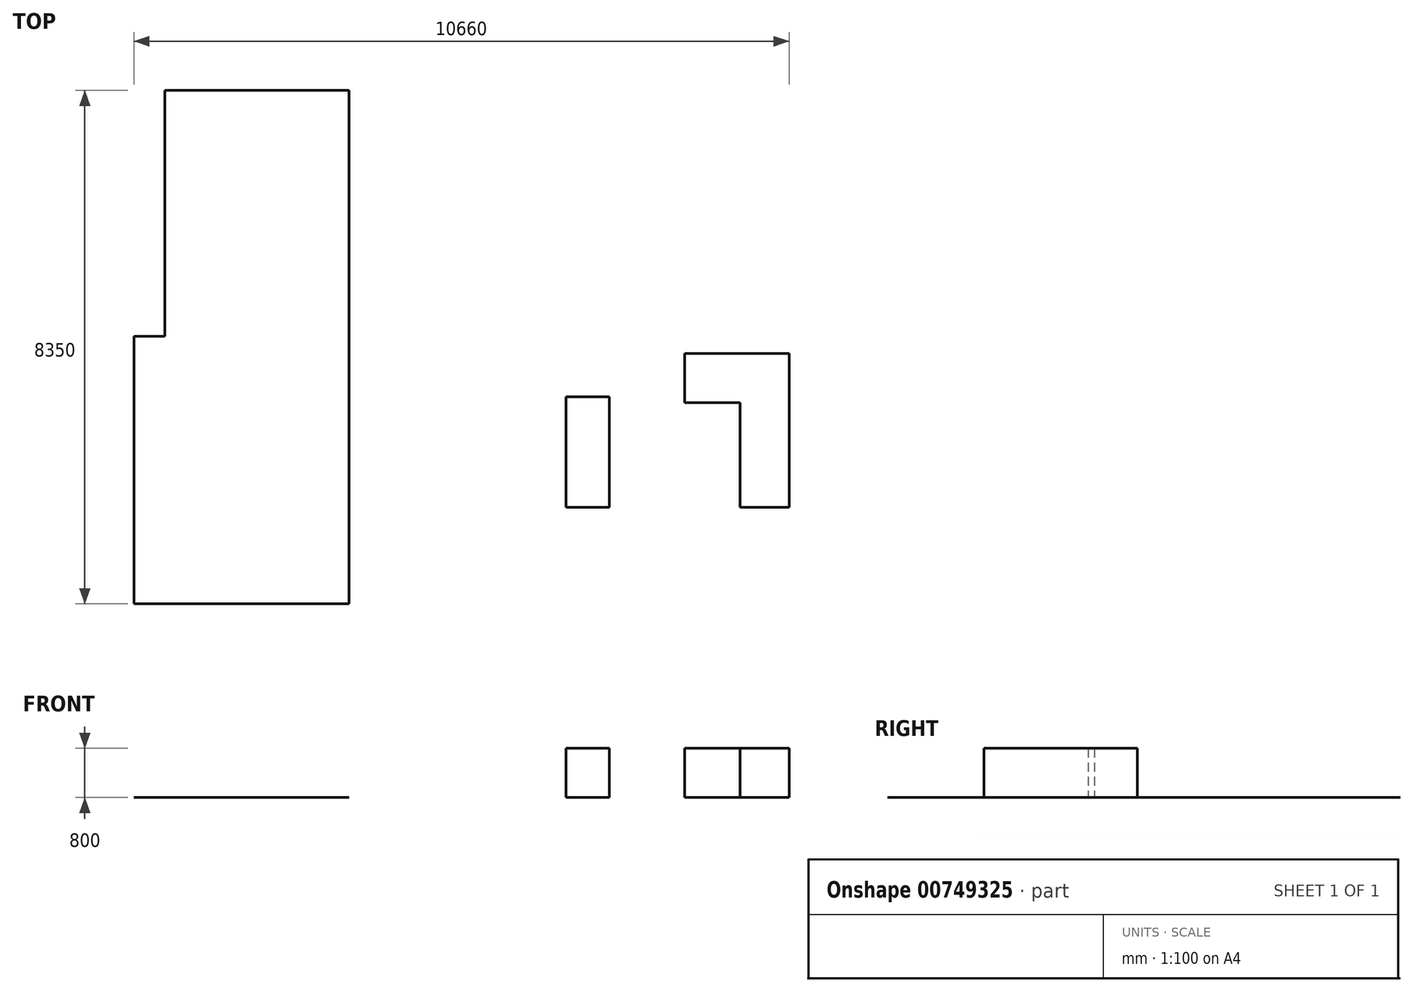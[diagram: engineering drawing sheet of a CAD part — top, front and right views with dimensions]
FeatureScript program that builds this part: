
annotation { "Feature Type Name" : "Feature", "Feature Type Description" : "" }
export const myFeature = defineFeature(function(context is Context, id is Id, definition is map)
    precondition{}
    {
        {
            var Q0;
            Q0=qCreatedBy(makeId("Top.planeOp"),FACE);
            var sketch = newSketch(context, id + "F0", { "sketchPlane" : qUnion([Q0])});
            skLineSegment(sketch, "E0", {"start": v(0, 0) * mm, "end": v(3500, 0) * mm});
            skLineSegment(sketch, "E1", {"start": v(3500, 0) * mm, "end": v(3500, 8350) * mm});
            skLineSegment(sketch, "E2", {"start": v(3500, 8350) * mm, "end": v(500, 8350) * mm});
            skLineSegment(sketch, "E3", {"start": v(500, 8350) * mm, "end": v(500, 4350) * mm});
            skLineSegment(sketch, "E4", {"start": v(500, 4350) * mm, "end": v(0, 4350) * mm});
            skLineSegment(sketch, "E5", {"start": v(0, 4350) * mm, "end": v(0, 0) * mm});
            skSolve(sketch);
        }
        {
            var Q0;
            Q0 = qSketchRegion(id + "F0", true);
            extrude(context, id + "F1", {"entities" : qUnion([Q0]), "depth" : 5 * mm, "offsetDistance" : 25 * mm});
        }
        {
            var Q0;
            Q0=qCreatedBy(makeId("Top.planeOp"),FACE);
            var sketch = newSketch(context, id + "F2", { "sketchPlane" : qUnion([Q0])});
            skLineSegment(sketch, "E6.bottom", {"start": v(7033.85, 3369.88) * mm, "end": v(7733.85, 3369.88) * mm});
            skLineSegment(sketch, "E6.top", {"start": v(7033.85, 1569.88) * mm, "end": v(7733.85, 1569.88) * mm});
            skLineSegment(sketch, "E6.left", {"start": v(7033.85, 3369.88) * mm, "end": v(7033.85, 1569.88) * mm});
            skLineSegment(sketch, "E6.right", {"start": v(7733.85, 3369.88) * mm, "end": v(7733.85, 1569.88) * mm});
            skLineSegment(sketch, "E7", {"start": v(10660, 1569.88) * mm, "end": v(10660, 4069.88) * mm});
            skLineSegment(sketch, "E8", {"start": v(10660, 4069.88) * mm, "end": v(8960, 4069.88) * mm});
            skLineSegment(sketch, "E9", {"start": v(8960, 4069.88) * mm, "end": v(8960, 3269.88) * mm});
            skLineSegment(sketch, "E10", {"start": v(8960, 3269.88) * mm, "end": v(9860, 3269.88) * mm});
            skLineSegment(sketch, "E11", {"start": v(9860, 3269.88) * mm, "end": v(9860, 1569.88) * mm});
            skLineSegment(sketch, "E12", {"start": v(9860, 1569.88) * mm, "end": v(10660, 1569.88) * mm});
            skSolve(sketch);
        }
        {
            var Q0;
            Q0=makeQuery(id+"F2.imprint","IMPRINT",FACE,{"disambiguationData":[TD([[makeQuery(id+"F2.imprint","IMPRINT",EDGE,{"derivedFrom":sQuery(id+"F2.wireOp",EDGE,"E6.bottom")}),-1.0]])]});
            var Q1;
            Q1=makeQuery(id+"F2.imprint","IMPRINT",FACE,{"disambiguationData":[TD([[makeQuery(id+"F2.imprint","IMPRINT",EDGE,{"derivedFrom":sQuery(id+"F2.wireOp",EDGE,"E7")}),1.0]])]});
            extrude(context, id + "F3", {"entities" : qUnion([Q0, Q1]), "depth" : 800 * mm, "offsetDistance" : 25 * mm});
        }
    });
